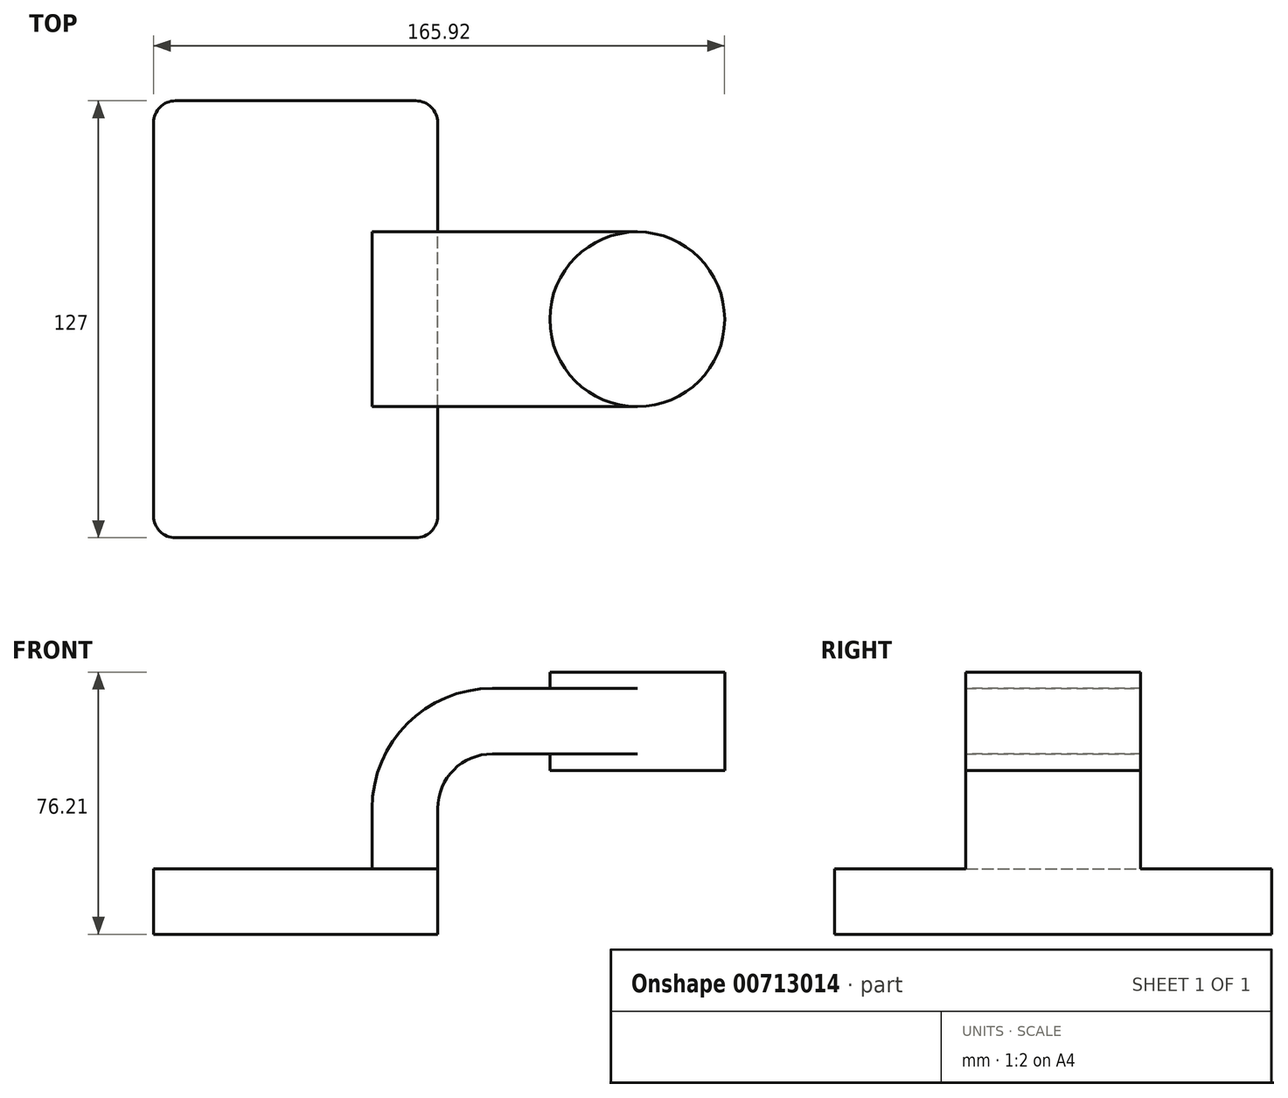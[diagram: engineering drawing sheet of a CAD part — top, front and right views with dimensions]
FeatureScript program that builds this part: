
annotation { "Feature Type Name" : "Feature", "Feature Type Description" : "" }
export const myFeature = defineFeature(function(context is Context, id is Id, definition is map)
    precondition{}
    {
        {
            var Q0;
            Q0=qCreatedBy(makeId("Front.planeOp"),FACE);
            var sketch = newSketch(context, id + "F0", { "sketchPlane" : qUnion([Q0])});
            skLineSegment(sketch, "E0.bottom", {"start": v(-41.28, -9.53) * mm, "end": v(41.28, -9.53) * mm});
            skLineSegment(sketch, "E0.top", {"start": v(-41.28, 9.52) * mm, "end": v(41.28, 9.52) * mm});
            skLineSegment(sketch, "E0.left", {"start": v(-41.27, -9.53) * mm, "end": v(-41.28, 9.52) * mm});
            skLineSegment(sketch, "E0.right", {"start": v(41.28, -9.53) * mm, "end": v(41.28, 9.52) * mm});
            skPoint(sketch, "E0.middle", {"position": v(0, 0) * mm});
            skLineSegment(sketch, "E1", {"start": v(41.27, 9.52) * mm, "end": v(41.27, 27) * mm});
            skArc(sketch, "E2", {"start": v(41.27, 27) * mm, "mid": v(45.92, 38.23) * mm, "end": v(57.15, 42.88) * mm});
            skLineSegment(sketch, "E3", {"start": v(57.15, 42.88) * mm, "end": v(99.25, 42.88) * mm});
            skLineSegment(sketch, "E4.bottom", {"start": v(124.65, 66.68) * mm, "end": v(73.85, 66.68) * mm});
            skLineSegment(sketch, "E4.top", {"start": v(124.65, 38.1) * mm, "end": v(73.85, 38.1) * mm});
            skLineSegment(sketch, "E4.left", {"start": v(124.65, 66.68) * mm, "end": v(124.65, 38.1) * mm});
            skLineSegment(sketch, "E4.right", {"start": v(73.85, 66.68) * mm, "end": v(73.85, 38.1) * mm});
            skPoint(sketch, "E4.middle", {"position": v(99.25, 52.39) * mm});
            skLineSegment(sketch, "E5.0", {"start": v(57.15, 61.93) * mm, "end": v(99.25, 61.93) * mm});
            skArc(sketch, "E5.1", {"start": v(22.22, 27) * mm, "mid": v(32.45, 51.7) * mm, "end": v(57.15, 61.93) * mm});
            skLineSegment(sketch, "E5.2", {"start": v(22.22, 9.52) * mm, "end": v(22.22, 27) * mm});
            skLineSegment(sketch, "E6", {"start": v(99.25, 66.68) * mm, "end": v(99.25, 38.1) * mm});
            skFitSpline(sketch, "E7", {"points": [v(-41.28, 9.52) * mm, v(57.15, 61.93) * mm], "startDerivative": vector(0.51, 101.52) * mm, "endDerivative": vector(120.26, -2.49) * mm});
            skSolve(sketch);
        }
        {
            var Q0;
            Q0=makeQuery(id+"F0.imprint","IMPRINT",FACE,{"disambiguationData":[TD([[makeQuery(id+"F0.imprint","IMPRINT",EDGE,{"derivedFrom":sQuery(id+"F0.wireOp",EDGE,"E0.bottom")}),1.0]])]});
            extrude(context, id + "F1", {"entities" : qUnion([Q0]), "endBound" : BoundingType.SYMMETRIC, "depth" : 127 * mm, "offsetDistance" : 25.4 * mm});
        }
        {
            var Q0;
            {var subQ5=sQuery(id+"F0.wireOp",EDGE,"E1");Q0=makeQuery(id+"F0.imprint","IMPRINT",FACE,{"disambiguationData":[TD([[makeQuery(id+"F0.imprint","IMPRINT",EDGE,{"derivedFrom":subQ5}),1.0]])]});}
            var Q1;
            {var subQ0=sQuery(id+"F0.wireOp",EDGE,"E6");var subQ1=sQuery(id+"F0.wireOp",EDGE,"E3");var subQ2=makeQuery(id+"F0.imprint","INTERSECT",VERTEX,{"derivedFrom":[subQ1,subQ0]});Q1=makeQuery(id+"F0.imprint","IMPRINT",FACE,{"disambiguationData":[TD([[makeQuery(id+"F0.imprint","IMPRINT",EDGE,{"disambiguationData":[TD([[subQ2,1.0]])],"derivedFrom":subQ1}),1.0]])]});}
            extrude(context, id + "F2", {"entities" : qUnion([Q0, Q1]), "operationType" : NewBodyOperationType.ADD, "endBound" : BoundingType.SYMMETRIC, "depth" : 50.8 * mm, "offsetDistance" : 25.4 * mm});
        }
        {
            var Q0;
            Q0=makeQuery(id+"F0.imprint","IMPRINT",FACE,{"disambiguationData":[TD([[makeQuery(id+"F0.imprint","IMPRINT",EDGE,{"derivedFrom":sQuery(id+"F0.wireOp",EDGE,"E5.1")}),1.0]])]});
            extrude(context, id + "F3", {"entities" : qUnion([Q0]), "operationType" : NewBodyOperationType.ADD, "endBound" : BoundingType.SYMMETRIC, "depth" : 15.88 * mm, "offsetDistance" : 25.4 * mm});
        }
        {
            var Q0;
            {var subQ0=sQuery(id+"F0.wireOp",EDGE,"E4.left");Q0=makeQuery(id+"F0.imprint","IMPRINT",FACE,{"disambiguationData":[TD([[makeQuery(id+"F0.imprint","IMPRINT",EDGE,{"derivedFrom":subQ0}),-1.0]])]});}
            var Q1;
            Q1=sQuery(id+"F0.wireOp",EDGE,"E6");
            revolve(context, id + "F4", {"operationType" : NewBodyOperationType.ADD, "surfaceOperationType" : NewSurfaceOperationType.NEW, "entities" : qUnion([Q0]), "axis" : qUnion([Q1]), "revolveType" : RevolveType.FULL});
        }
        {
            var Q0;
            Q0=makeQuery(id+"F1.opExtrude","CAP_EDGE",EDGE,{"disambiguationData":[OSD([sQuery(id+"F0.wireOp",EDGE,"E0.right")])],"isStart":false});
            var Q1;
            Q1=makeQuery(id+"F1.opExtrude","CAP_EDGE",EDGE,{"disambiguationData":[OSD([sQuery(id+"F0.wireOp",EDGE,"E0.left")])],"isStart":false});
            var Q2;
            Q2=makeQuery(id+"F1.opExtrude","CAP_EDGE",EDGE,{"disambiguationData":[OSD([sQuery(id+"F0.wireOp",EDGE,"E0.left")])],"isStart":true});
            var Q3;
            Q3=makeQuery(id+"F1.opExtrude","CAP_EDGE",EDGE,{"disambiguationData":[OSD([sQuery(id+"F0.wireOp",EDGE,"E0.right")])],"isStart":true});
            fillet(context, id + "F5", {"entities" : qUnion([Q0, Q1, Q2, Q3]), "radius" : 6.35 * mm, "tangentPropagation" : true, "allowEdgeOverflow" : false});
        }
    });
